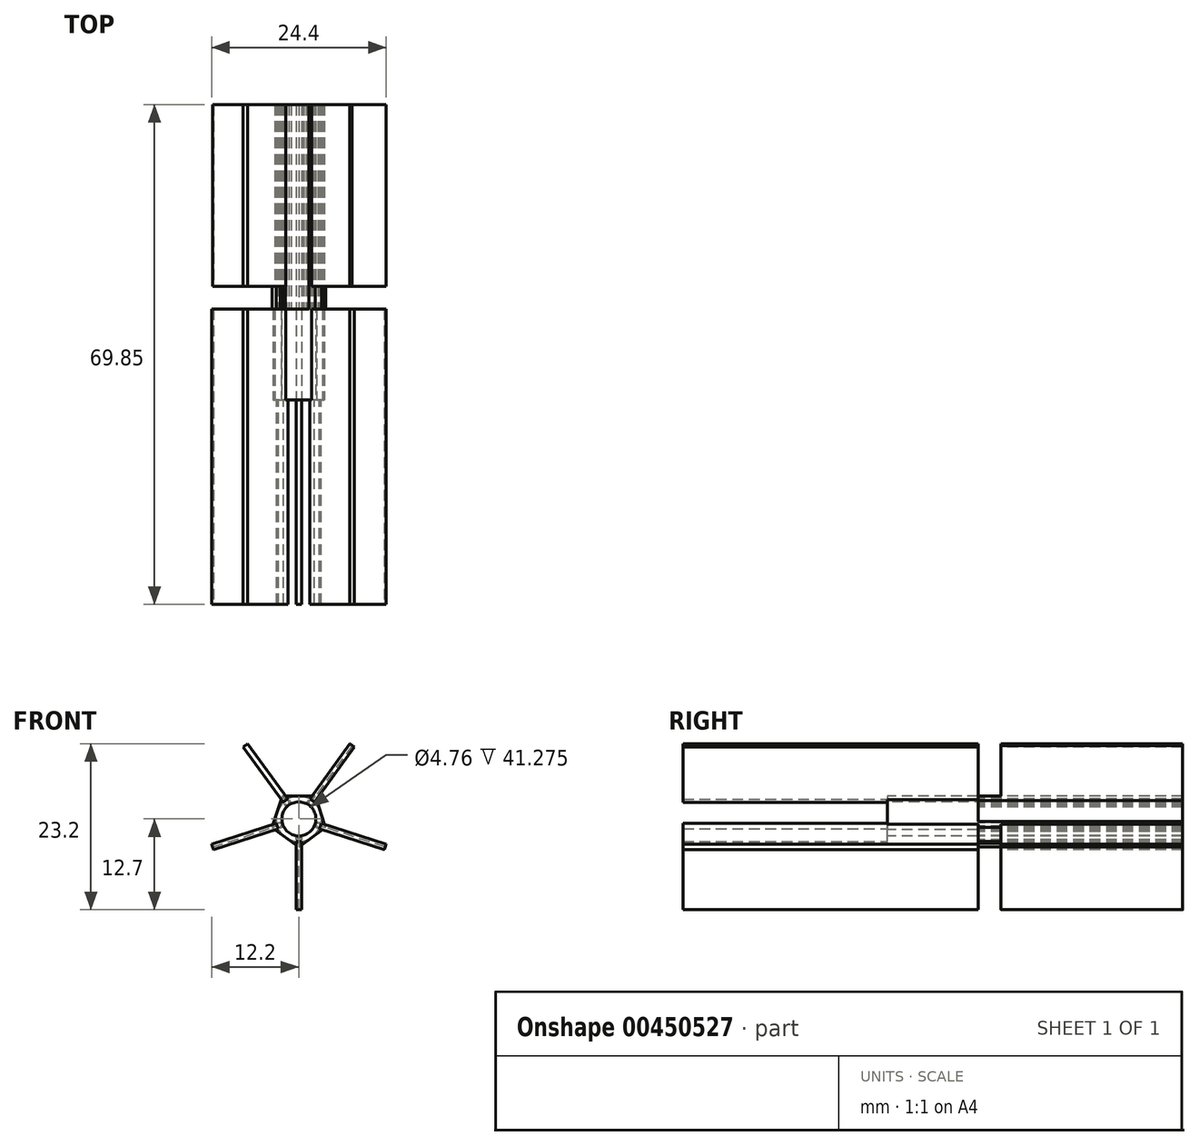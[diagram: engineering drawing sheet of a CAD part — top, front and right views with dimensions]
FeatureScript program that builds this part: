
annotation { "Feature Type Name" : "Feature", "Feature Type Description" : "" }
export const myFeature = defineFeature(function(context is Context, id is Id, definition is map)
    precondition{}
    {
        {
            var Q0;
            Q0=qCreatedBy(makeId("Front.planeOp"),FACE);
            var sketch = newSketch(context, id + "F0", { "sketchPlane" : qUnion([Q0])});
            skLineSegment(sketch, "E0", {"start": v(0, 0) * mm, "end": v(-7.46, 10.27) * mm});
            skLineSegment(sketch, "E1", {"start": v(0, 0) * mm, "end": v(7.46, 10.27) * mm});
            skArc(sketch, "E2", {"start": v(7.46, 10.27) * mm, "mid": v(0, 12.7) * mm, "end": v(-7.46, 10.27) * mm});
            skCircle(sketch, "E3", {"center": v(0, 7.62) * mm, "radius": 3.97 * mm});
            skCircle(sketch, "E4", {"center": v(0, 7.62) * mm, "radius": 3.66 * mm});
            skCircle(sketch, "E5", {"center": v(0, 7.62) * mm, "radius": 2.76 * mm});
            skLineSegment(sketch, "E6", {"start": v(3.41, 5.37) * mm, "end": v(7.14, 10.5) * mm});
            skLineSegment(sketch, "E7", {"start": v(3.41, 5.37) * mm, "end": v(0, 0.68) * mm});
            skLineSegment(sketch, "E8", {"start": v(-3.41, 5.37) * mm, "end": v(-7.14, 10.5) * mm});
            skLineSegment(sketch, "E9", {"start": v(-3.41, 5.37) * mm, "end": v(0, 0.68) * mm});
            skLineSegment(sketch, "E10", {"start": v(0, 3.17) * mm, "end": v(2.3, 3.17) * mm});
            skLineSegment(sketch, "E11", {"start": v(0, 3.17) * mm, "end": v(-2.3, 3.17) * mm});
            skLineSegment(sketch, "E12", {"start": v(0, 11.28) * mm, "end": v(5.84, 11.28) * mm});
            skLineSegment(sketch, "E13", {"start": v(0, 11.28) * mm, "end": v(-5.84, 11.28) * mm});
            skPoint(sketch, "E14.orphan", {"position": v(0, 12.7) * mm});
            skArc(sketch, "E15", {"start": v(1.87, 2.57) * mm, "mid": v(0, 3.17) * mm, "end": v(-1.87, 2.57) * mm});
            skArc(sketch, "E16", {"start": v(-5.6, 7.7) * mm, "mid": v(-4.37, 9.58) * mm, "end": v(-4.68, 11.8) * mm});
            skArc(sketch, "E17", {"start": v(4.68, 11.8) * mm, "mid": v(4.37, 9.58) * mm, "end": v(5.6, 7.7) * mm});
            skLineSegment(sketch, "E18", {"start": v(0, 7.62) * mm, "end": v(-5.54, 7.62) * mm});
            skLineSegment(sketch, "E19", {"start": v(0, 7.62) * mm, "end": v(5.54, 7.62) * mm});
            skArc(sketch, "E20", {"start": v(1.4, 1.93) * mm, "mid": v(0, 2.38) * mm, "end": v(-1.4, 1.93) * mm});
            skLineSegment(sketch, "E21", {"start": v(-1.4, 1.93) * mm, "end": v(-1.4, 3.17) * mm});
            skLineSegment(sketch, "E22", {"start": v(1.4, 1.93) * mm, "end": v(1.4, 3.17) * mm});
            skSolve(sketch);
        }
        {
            var Q0;
            Q0=qCreatedBy(makeId("Top.planeOp"),FACE);
            var sketch = newSketch(context, id + "F1", { "sketchPlane" : qUnion([Q0])});
            skLineSegment(sketch, "E23", {"start": v(0, 0) * mm, "end": v(0, 12.7) * mm});
            skSolve(sketch);
        }
        {
            var Q0;
            {var subQ0=sQuery(id+"F0.wireOp",EDGE,"E10");var subQ1=sQuery(id+"F0.wireOp",EDGE,"E1");var subQ2=makeQuery(id+"F0.imprint","INTERSECT",VERTEX,{"derivedFrom":[subQ1,subQ0]});Q0=makeQuery(id+"F0.imprint","IMPRINT",FACE,{"disambiguationData":[TD([[makeQuery(id+"F0.imprint","IMPRINT",EDGE,{"disambiguationData":[TD([[subQ2,-1.0]])],"derivedFrom":subQ1}),1.0]])]});}
            var Q1;
            {var subQ0=sQuery(id+"F0.wireOp",EDGE,"E11");var subQ1=sQuery(id+"F0.wireOp",EDGE,"E0");var subQ2=makeQuery(id+"F0.imprint","INTERSECT",VERTEX,{"derivedFrom":[subQ1,subQ0]});Q1=makeQuery(id+"F0.imprint","IMPRINT",FACE,{"disambiguationData":[TD([[makeQuery(id+"F0.imprint","IMPRINT",EDGE,{"disambiguationData":[TD([[subQ2,-1.0]])],"derivedFrom":subQ1}),-1.0]])]});}
            var Q2;
            {var subQ0=sQuery(id+"F0.wireOp",EDGE,"E10");var subQ1=sQuery(id+"F0.wireOp",EDGE,"E1");var subQ2=makeQuery(id+"F0.imprint","INTERSECT",VERTEX,{"derivedFrom":[subQ1,subQ0]});Q2=makeQuery(id+"F0.imprint","IMPRINT",FACE,{"disambiguationData":[TD([[makeQuery(id+"F0.imprint","IMPRINT",EDGE,{"disambiguationData":[TD([[subQ2,1.0]])],"derivedFrom":subQ1}),1.0]])]});}
            var Q3;
            {var subQ0=sQuery(id+"F0.wireOp",EDGE,"E10");var subQ1=sQuery(id+"F0.wireOp",EDGE,"E7");var subQ2=makeQuery(id+"F0.imprint","INTERSECT",VERTEX,{"derivedFrom":[subQ1,subQ0]});Q3=makeQuery(id+"F0.imprint","IMPRINT",FACE,{"disambiguationData":[TD([[makeQuery(id+"F0.imprint","IMPRINT",EDGE,{"disambiguationData":[TD([[subQ2,-1.0]])],"derivedFrom":subQ1}),-1.0]])]});}
            var Q4;
            {var subQ0=sQuery(id+"F0.wireOp",EDGE,"E11");var subQ1=sQuery(id+"F0.wireOp",EDGE,"E9");var subQ2=makeQuery(id+"F0.imprint","INTERSECT",VERTEX,{"derivedFrom":[subQ1,subQ0]});Q4=makeQuery(id+"F0.imprint","IMPRINT",FACE,{"disambiguationData":[TD([[makeQuery(id+"F0.imprint","IMPRINT",EDGE,{"disambiguationData":[TD([[subQ2,-1.0]])],"derivedFrom":subQ1}),1.0]])]});}
            var Q5;
            {var subQ0=sQuery(id+"F0.wireOp",EDGE,"E11");var subQ1=sQuery(id+"F0.wireOp",EDGE,"E0");var subQ2=makeQuery(id+"F0.imprint","INTERSECT",VERTEX,{"derivedFrom":[subQ1,subQ0]});Q5=makeQuery(id+"F0.imprint","IMPRINT",FACE,{"disambiguationData":[TD([[makeQuery(id+"F0.imprint","IMPRINT",EDGE,{"disambiguationData":[TD([[subQ2,1.0]])],"derivedFrom":subQ1}),-1.0]])]});}
            var Q6;
            {var subQ0=sQuery(id+"F0.wireOp",EDGE,"E15");var subQ1=sQuery(id+"F0.wireOp",EDGE,"E1");var subQ2=makeQuery(id+"F0.imprint","INTERSECT",VERTEX,{"derivedFrom":[subQ1,subQ0]});Q6=makeQuery(id+"F0.imprint","IMPRINT",FACE,{"disambiguationData":[TD([[makeQuery(id+"F0.imprint","IMPRINT",EDGE,{"disambiguationData":[TD([[subQ2,1.0]])],"derivedFrom":subQ1}),1.0]])]});}
            var Q7;
            {var subQ0=sQuery(id+"F0.wireOp",EDGE,"E15");var subQ6=sQuery(id+"F0.wireOp",EDGE,"E7");var subQ8=makeQuery(id+"F0.imprint","INTERSECT",VERTEX,{"derivedFrom":[subQ6,subQ0]});Q7=makeQuery(id+"F0.imprint","IMPRINT",FACE,{"disambiguationData":[TD([[makeQuery(id+"F0.imprint","IMPRINT",EDGE,{"disambiguationData":[TD([[subQ8,-1.0]])],"derivedFrom":subQ6}),-1.0]])]});}
            var Q8;
            {var subQ0=sQuery(id+"F0.wireOp",EDGE,"E15");var subQ1=sQuery(id+"F0.wireOp",EDGE,"E0");var subQ2=makeQuery(id+"F0.imprint","INTERSECT",VERTEX,{"derivedFrom":[subQ1,subQ0]});Q8=makeQuery(id+"F0.imprint","IMPRINT",FACE,{"disambiguationData":[TD([[makeQuery(id+"F0.imprint","IMPRINT",EDGE,{"disambiguationData":[TD([[subQ2,1.0]])],"derivedFrom":subQ1}),-1.0]])]});}
            var Q9;
            {var subQ0=sQuery(id+"F0.wireOp",EDGE,"E17");var subQ1=sQuery(id+"F0.wireOp",EDGE,"E1");var subQ2=makeQuery(id+"F0.imprint","INTERSECT",VERTEX,{"derivedFrom":[subQ1,subQ0]});Q9=makeQuery(id+"F0.imprint","IMPRINT",FACE,{"disambiguationData":[TD([[makeQuery(id+"F0.imprint","IMPRINT",EDGE,{"disambiguationData":[TD([[subQ2,1.0]])],"derivedFrom":subQ1}),1.0]])]});}
            var Q10;
            {var subQ0=sQuery(id+"F0.wireOp",EDGE,"E16");var subQ1=sQuery(id+"F0.wireOp",EDGE,"E0");var subQ2=makeQuery(id+"F0.imprint","INTERSECT",VERTEX,{"derivedFrom":[subQ1,subQ0]});Q10=makeQuery(id+"F0.imprint","IMPRINT",FACE,{"disambiguationData":[TD([[makeQuery(id+"F0.imprint","IMPRINT",EDGE,{"disambiguationData":[TD([[subQ2,1.0]])],"derivedFrom":subQ1}),-1.0]])]});}
            var Q11;
            {var subQ0=sQuery(id+"F0.wireOp",EDGE,"E15");var subQ1=sQuery(id+"F0.wireOp",EDGE,"E9");var subQ2=makeQuery(id+"F0.imprint","INTERSECT",VERTEX,{"derivedFrom":[subQ1,subQ0]});Q11=makeQuery(id+"F0.imprint","IMPRINT",FACE,{"disambiguationData":[TD([[makeQuery(id+"F0.imprint","IMPRINT",EDGE,{"disambiguationData":[TD([[subQ2,-1.0]])],"derivedFrom":subQ1}),1.0]])]});}
            var Q12;
            {var subQ0=sQuery(id+"F0.wireOp",EDGE,"E21");var subQ1=sQuery(id+"F0.wireOp",EDGE,"E9");var subQ2=makeQuery(id+"F0.imprint","INTERSECT",VERTEX,{"derivedFrom":[subQ1,subQ0]});Q12=makeQuery(id+"F0.imprint","IMPRINT",FACE,{"disambiguationData":[TD([[makeQuery(id+"F0.imprint","IMPRINT",EDGE,{"disambiguationData":[TD([[subQ2,-1.0]])],"derivedFrom":subQ1}),-1.0]])]});}
            var Q13;
            {var subQ0=sQuery(id+"F0.wireOp",EDGE,"E22");var subQ1=sQuery(id+"F0.wireOp",EDGE,"E7");var subQ2=makeQuery(id+"F0.imprint","INTERSECT",VERTEX,{"derivedFrom":[subQ1,subQ0]});Q13=makeQuery(id+"F0.imprint","IMPRINT",FACE,{"disambiguationData":[TD([[makeQuery(id+"F0.imprint","IMPRINT",EDGE,{"disambiguationData":[TD([[subQ2,-1.0]])],"derivedFrom":subQ1}),1.0]])]});}
            var Q14;
            {var subQ2=sQuery(id+"F0.wireOp",EDGE,"E22");var subQ10=sQuery(id+"F0.wireOp",EDGE,"E7");var subQ11=makeQuery(id+"F0.imprint","INTERSECT",VERTEX,{"derivedFrom":[subQ10,subQ2]});Q14=makeQuery(id+"F0.imprint","IMPRINT",FACE,{"disambiguationData":[TD([[makeQuery(id+"F0.imprint","IMPRINT",EDGE,{"disambiguationData":[TD([[subQ11,-1.0]])],"derivedFrom":subQ10}),-1.0]])]});}
            var Q15;
            {var subQ1=sQuery(id+"F0.wireOp",EDGE,"E11");var subQ3=sQuery(id+"F0.wireOp",EDGE,"E21");var subQ4=makeQuery(id+"F0.imprint","INTERSECT",VERTEX,{"derivedFrom":[subQ1,subQ3]});Q15=makeQuery(id+"F0.imprint","IMPRINT",FACE,{"disambiguationData":[TD([[makeQuery(id+"F0.imprint","IMPRINT",EDGE,{"disambiguationData":[TD([[subQ4,1.0]])],"derivedFrom":subQ3}),-1.0]])]});}
            var Q16;
            {var subQ1=sQuery(id+"F0.wireOp",EDGE,"E10");var subQ3=sQuery(id+"F0.wireOp",EDGE,"E22");var subQ4=makeQuery(id+"F0.imprint","INTERSECT",VERTEX,{"derivedFrom":[subQ1,subQ3]});Q16=makeQuery(id+"F0.imprint","IMPRINT",FACE,{"disambiguationData":[TD([[makeQuery(id+"F0.imprint","IMPRINT",EDGE,{"disambiguationData":[TD([[subQ4,1.0]])],"derivedFrom":subQ3}),1.0]])]});}
            var Q17;
            {var subQ0=sQuery(id+"F0.wireOp",EDGE,"E2");var subQ1=sQuery(id+"F0.wireOp",EDGE,"E1");var subQ2=makeQuery(id+"F0.imprint","INTERSECT",VERTEX,{"derivedFrom":[subQ1,subQ0]});Q17=makeQuery(id+"F0.imprint","IMPRINT",FACE,{"disambiguationData":[TD([[makeQuery(id+"F0.imprint","IMPRINT",EDGE,{"disambiguationData":[TD([[subQ2,1.0]])],"derivedFrom":subQ1}),1.0]])]});}
            var Q18;
            {var subQ0=sQuery(id+"F0.wireOp",EDGE,"E2");var subQ1=sQuery(id+"F0.wireOp",EDGE,"E0");var subQ2=makeQuery(id+"F0.imprint","INTERSECT",VERTEX,{"derivedFrom":[subQ1,subQ0]});Q18=makeQuery(id+"F0.imprint","IMPRINT",FACE,{"disambiguationData":[TD([[makeQuery(id+"F0.imprint","IMPRINT",EDGE,{"disambiguationData":[TD([[subQ2,1.0]])],"derivedFrom":subQ1}),-1.0]])]});}
            extrude(context, id + "F2", {"entities" : qUnion([Q0, Q1, Q2, Q3, Q4, Q5, Q6, Q7, Q8, Q9, Q10, Q11, Q12, Q13, Q14, Q15, Q16, Q17, Q18]), "oppositeDirection" : true, "depth" : 12.7 * mm});
        }
        {
            var Q0;
            {var subQ0=sQuery(id+"F0.wireOp",EDGE,"E11");var subQ1=sQuery(id+"F0.wireOp",EDGE,"E0");var subQ2=makeQuery(id+"F0.imprint","INTERSECT",VERTEX,{"derivedFrom":[subQ1,subQ0]});Q0=makeQuery(id+"F0.imprint","IMPRINT",FACE,{"disambiguationData":[TD([[makeQuery(id+"F0.imprint","IMPRINT",EDGE,{"disambiguationData":[TD([[subQ2,-1.0]])],"derivedFrom":subQ1}),-1.0]])]});}
            var Q1;
            {var subQ0=sQuery(id+"F0.wireOp",EDGE,"E11");var subQ1=sQuery(id+"F0.wireOp",EDGE,"E0");var subQ2=makeQuery(id+"F0.imprint","INTERSECT",VERTEX,{"derivedFrom":[subQ1,subQ0]});Q1=makeQuery(id+"F0.imprint","IMPRINT",FACE,{"disambiguationData":[TD([[makeQuery(id+"F0.imprint","IMPRINT",EDGE,{"disambiguationData":[TD([[subQ2,1.0]])],"derivedFrom":subQ1}),-1.0]])]});}
            var Q2;
            {var subQ0=sQuery(id+"F0.wireOp",EDGE,"E10");var subQ1=sQuery(id+"F0.wireOp",EDGE,"E1");var subQ2=makeQuery(id+"F0.imprint","INTERSECT",VERTEX,{"derivedFrom":[subQ1,subQ0]});Q2=makeQuery(id+"F0.imprint","IMPRINT",FACE,{"disambiguationData":[TD([[makeQuery(id+"F0.imprint","IMPRINT",EDGE,{"disambiguationData":[TD([[subQ2,1.0]])],"derivedFrom":subQ1}),1.0]])]});}
            var Q3;
            {var subQ3=sQuery(id+"F0.wireOp",EDGE,"E10");var subQ5=sQuery(id+"F0.wireOp",EDGE,"E1");var subQ6=makeQuery(id+"F0.imprint","INTERSECT",VERTEX,{"derivedFrom":[subQ5,subQ3]});Q3=makeQuery(id+"F0.imprint","IMPRINT",FACE,{"disambiguationData":[TD([[makeQuery(id+"F0.imprint","IMPRINT",EDGE,{"disambiguationData":[TD([[subQ6,-1.0]])],"derivedFrom":subQ5}),1.0]])]});}
            var Q4;
            {var subQ0=sQuery(id+"F0.wireOp",EDGE,"E17");var subQ1=sQuery(id+"F0.wireOp",EDGE,"E1");var subQ2=makeQuery(id+"F0.imprint","INTERSECT",VERTEX,{"derivedFrom":[subQ1,subQ0]});Q4=makeQuery(id+"F0.imprint","IMPRINT",FACE,{"disambiguationData":[TD([[makeQuery(id+"F0.imprint","IMPRINT",EDGE,{"disambiguationData":[TD([[subQ2,1.0]])],"derivedFrom":subQ1}),1.0]])]});}
            var Q5;
            {var subQ0=sQuery(id+"F0.wireOp",EDGE,"E16");var subQ1=sQuery(id+"F0.wireOp",EDGE,"E0");var subQ2=makeQuery(id+"F0.imprint","INTERSECT",VERTEX,{"derivedFrom":[subQ1,subQ0]});Q5=makeQuery(id+"F0.imprint","IMPRINT",FACE,{"disambiguationData":[TD([[makeQuery(id+"F0.imprint","IMPRINT",EDGE,{"disambiguationData":[TD([[subQ2,1.0]])],"derivedFrom":subQ1}),-1.0]])]});}
            var Q6;
            {var subQ0=sQuery(id+"F0.wireOp",EDGE,"E2");var subQ1=sQuery(id+"F0.wireOp",EDGE,"E0");var subQ2=makeQuery(id+"F0.imprint","INTERSECT",VERTEX,{"derivedFrom":[subQ1,subQ0]});Q6=makeQuery(id+"F0.imprint","IMPRINT",FACE,{"disambiguationData":[TD([[makeQuery(id+"F0.imprint","IMPRINT",EDGE,{"disambiguationData":[TD([[subQ2,1.0]])],"derivedFrom":subQ1}),-1.0]])]});}
            var Q7;
            {var subQ0=sQuery(id+"F0.wireOp",EDGE,"E2");var subQ1=sQuery(id+"F0.wireOp",EDGE,"E1");var subQ2=makeQuery(id+"F0.imprint","INTERSECT",VERTEX,{"derivedFrom":[subQ1,subQ0]});Q7=makeQuery(id+"F0.imprint","IMPRINT",FACE,{"disambiguationData":[TD([[makeQuery(id+"F0.imprint","IMPRINT",EDGE,{"disambiguationData":[TD([[subQ2,1.0]])],"derivedFrom":subQ1}),1.0]])]});}
            extrude(context, id + "F3", {"entities" : qUnion([Q0, Q1, Q2, Q3, Q4, Q5, Q6, Q7]), "operationType" : NewBodyOperationType.ADD, "depth" : 28.57 * mm});
        }
        {
            var Q0;
            Q0=makeQuery(id+"F2.opExtrude","CAP_FACE",FACE,{"disambiguationData":[OSD([sQuery(id+"F0.wireOp",EDGE,"E0"),sQuery(id+"F0.wireOp",EDGE,"E1"),sQuery(id+"F0.wireOp",EDGE,"E2"),sQuery(id+"F0.wireOp",EDGE,"E6"),sQuery(id+"F0.wireOp",EDGE,"E7"),sQuery(id+"F0.wireOp",EDGE,"E8"),sQuery(id+"F0.wireOp",EDGE,"E9"),sQuery(id+"F0.wireOp",EDGE,"E10"),sQuery(id+"F0.wireOp",EDGE,"E11"),sQuery(id+"F0.wireOp",EDGE,"E20")])],"isStart":false});
            var sketch = newSketch(context, id + "F4", { "sketchPlane" : qUnion([Q0])});
            skArc(sketch, "E24.0.0", {"start": v(-1.53, 2.78) * mm, "mid": v(-1.7, 2.68) * mm, "end": v(-1.87, 2.57) * mm});
            skLineSegment(sketch, "E24.0.1", {"start": v(-1.87, 2.57) * mm, "end": v(-2.3, 3.17) * mm});
            skLineSegment(sketch, "E24.0.2", {"start": v(-2.3, 3.17) * mm, "end": v(-1.82, 3.17) * mm});
            skLineSegment(sketch, "E24.0.3", {"start": v(-1.82, 3.17) * mm, "end": v(-1.53, 2.78) * mm});
            skLineSegment(sketch, "E25.0.0", {"start": v(-1.4, 3.17) * mm, "end": v(-1.4, 2.85) * mm});
            skArc(sketch, "E25.0.1", {"start": v(-1.4, 2.85) * mm, "mid": v(-1.47, 2.82) * mm, "end": v(-1.53, 2.78) * mm});
            skLineSegment(sketch, "E25.0.2", {"start": v(-1.53, 2.78) * mm, "end": v(-1.82, 3.17) * mm});
            skLineSegment(sketch, "E25.0.3", {"start": v(-1.82, 3.17) * mm, "end": v(-1.4, 3.17) * mm});
            skLineSegment(sketch, "E26.0.0", {"start": v(-1.4, 2.6) * mm, "end": v(-1.4, 2.85) * mm});
            skArc(sketch, "E26.0.1", {"start": v(-1.4, 2.85) * mm, "mid": v(-0.72, 3.1) * mm, "end": v(0, 3.18) * mm});
            skArc(sketch, "E26.0.2", {"start": v(0, 3.18) * mm, "mid": v(0.72, 3.1) * mm, "end": v(1.4, 2.85) * mm});
            skLineSegment(sketch, "E26.0.3", {"start": v(1.4, 2.85) * mm, "end": v(1.4, 2.6) * mm});
            skLineSegment(sketch, "E26.0.4", {"start": v(1.4, 2.6) * mm, "end": v(1.06, 2.13) * mm});
            skArc(sketch, "E26.0.5", {"start": v(1.06, 2.13) * mm, "mid": v(0, 2.38) * mm, "end": v(-1.06, 2.13) * mm});
            skLineSegment(sketch, "E26.0.6", {"start": v(-1.06, 2.13) * mm, "end": v(-1.4, 2.6) * mm});
            skArc(sketch, "E27.0.0", {"start": v(0, 3.18) * mm, "mid": v(-0.72, 3.1) * mm, "end": v(-1.4, 2.85) * mm});
            skLineSegment(sketch, "E27.0.1", {"start": v(-1.4, 2.85) * mm, "end": v(-1.4, 3.17) * mm});
            skLineSegment(sketch, "E27.0.2", {"start": v(-1.4, 3.17) * mm, "end": v(0, 3.17) * mm});
            skArc(sketch, "E28.0.0", {"start": v(1.4, 2.85) * mm, "mid": v(0.72, 3.1) * mm, "end": v(0, 3.18) * mm});
            skLineSegment(sketch, "E28.0.1", {"start": v(0, 3.17) * mm, "end": v(1.4, 3.17) * mm});
            skLineSegment(sketch, "E28.0.2", {"start": v(1.4, 3.17) * mm, "end": v(1.4, 2.85) * mm});
            skLineSegment(sketch, "E29.0.0", {"start": v(1.4, 2.85) * mm, "end": v(1.4, 3.17) * mm});
            skLineSegment(sketch, "E29.0.1", {"start": v(1.4, 3.17) * mm, "end": v(1.82, 3.17) * mm});
            skLineSegment(sketch, "E29.0.2", {"start": v(1.82, 3.17) * mm, "end": v(1.53, 2.78) * mm});
            skArc(sketch, "E29.0.3", {"start": v(1.53, 2.78) * mm, "mid": v(1.47, 2.82) * mm, "end": v(1.4, 2.85) * mm});
            skLineSegment(sketch, "E30.0.0", {"start": v(1.53, 2.78) * mm, "end": v(1.82, 3.17) * mm});
            skLineSegment(sketch, "E30.0.1", {"start": v(1.82, 3.17) * mm, "end": v(2.3, 3.17) * mm});
            skLineSegment(sketch, "E30.0.2", {"start": v(2.3, 3.17) * mm, "end": v(1.87, 2.57) * mm});
            skArc(sketch, "E30.0.3", {"start": v(1.87, 2.57) * mm, "mid": v(1.7, 2.68) * mm, "end": v(1.53, 2.78) * mm});
            skLineSegment(sketch, "E31.0.0", {"start": v(1.4, 2.6) * mm, "end": v(1.53, 2.78) * mm});
            skArc(sketch, "E31.0.1", {"start": v(1.53, 2.78) * mm, "mid": v(1.7, 2.68) * mm, "end": v(1.87, 2.57) * mm});
            skLineSegment(sketch, "E31.0.2", {"start": v(1.87, 2.57) * mm, "end": v(1.4, 1.93) * mm});
            skLineSegment(sketch, "E31.0.3", {"start": v(1.4, 1.93) * mm, "end": v(1.4, 2.6) * mm});
            skLineSegment(sketch, "E32.0.0", {"start": v(1.4, 2.6) * mm, "end": v(1.4, 1.93) * mm});
            skArc(sketch, "E32.0.1", {"start": v(1.4, 1.93) * mm, "mid": v(1.23, 2.04) * mm, "end": v(1.06, 2.13) * mm});
            skLineSegment(sketch, "E32.0.2", {"start": v(1.06, 2.13) * mm, "end": v(1.4, 2.6) * mm});
            skLineSegment(sketch, "E33.0.0", {"start": v(-1.4, 1.93) * mm, "end": v(-1.87, 2.57) * mm});
            skArc(sketch, "E33.0.1", {"start": v(-1.87, 2.57) * mm, "mid": v(-1.7, 2.68) * mm, "end": v(-1.53, 2.78) * mm});
            skLineSegment(sketch, "E33.0.2", {"start": v(-1.53, 2.78) * mm, "end": v(-1.4, 2.6) * mm});
            skLineSegment(sketch, "E33.0.3", {"start": v(-1.4, 2.6) * mm, "end": v(-1.4, 1.93) * mm});
            skLineSegment(sketch, "E34.0.0", {"start": v(-1.4, 1.93) * mm, "end": v(-1.4, 2.6) * mm});
            skLineSegment(sketch, "E34.0.1", {"start": v(-1.4, 2.6) * mm, "end": v(-1.06, 2.13) * mm});
            skArc(sketch, "E34.0.2", {"start": v(-1.06, 2.13) * mm, "mid": v(-1.23, 2.04) * mm, "end": v(-1.4, 1.93) * mm});
            skLineSegment(sketch, "E35.0.0", {"start": v(-7.14, 10.5) * mm, "end": v(-5.3, 7.96) * mm});
            skArc(sketch, "E35.0.1", {"start": v(-5.3, 7.96) * mm, "mid": v(-5.44, 7.83) * mm, "end": v(-5.6, 7.7) * mm});
            skLineSegment(sketch, "E35.0.2", {"start": v(-5.6, 7.7) * mm, "end": v(-7.46, 10.27) * mm});
            skArc(sketch, "E35.0.3", {"start": v(-7.46, 10.27) * mm, "mid": v(-7.3, 10.39) * mm, "end": v(-7.14, 10.5) * mm});
            skArc(sketch, "E36.0.0", {"start": v(-5.6, 7.7) * mm, "mid": v(-5.44, 7.83) * mm, "end": v(-5.3, 7.96) * mm});
            skLineSegment(sketch, "E36.0.1", {"start": v(-5.3, 7.96) * mm, "end": v(-5.05, 7.62) * mm});
            skLineSegment(sketch, "E36.0.2", {"start": v(-5.05, 7.62) * mm, "end": v(-5.54, 7.62) * mm});
            skLineSegment(sketch, "E36.0.3", {"start": v(-5.54, 7.62) * mm, "end": v(-5.6, 7.7) * mm});
            skLineSegment(sketch, "E37.0.0", {"start": v(-5.54, 7.62) * mm, "end": v(-5.05, 7.62) * mm});
            skLineSegment(sketch, "E37.0.1", {"start": v(-5.05, 7.62) * mm, "end": v(-3.41, 5.37) * mm});
            skLineSegment(sketch, "E37.0.2", {"start": v(-3.41, 5.37) * mm, "end": v(-1.82, 3.17) * mm});
            skLineSegment(sketch, "E37.0.3", {"start": v(-1.82, 3.17) * mm, "end": v(-2.3, 3.17) * mm});
            skLineSegment(sketch, "E37.0.4", {"start": v(-2.3, 3.17) * mm, "end": v(-5.54, 7.62) * mm});
            skLineSegment(sketch, "E38.0.0", {"start": v(7.46, 10.27) * mm, "end": v(5.6, 7.7) * mm});
            skArc(sketch, "E38.0.1", {"start": v(5.6, 7.7) * mm, "mid": v(5.44, 7.83) * mm, "end": v(5.3, 7.96) * mm});
            skLineSegment(sketch, "E38.0.2", {"start": v(5.3, 7.96) * mm, "end": v(7.14, 10.5) * mm});
            skArc(sketch, "E38.0.3", {"start": v(7.14, 10.5) * mm, "mid": v(7.3, 10.39) * mm, "end": v(7.46, 10.27) * mm});
            skArc(sketch, "E39.0.0", {"start": v(5.3, 7.96) * mm, "mid": v(5.44, 7.83) * mm, "end": v(5.6, 7.7) * mm});
            skLineSegment(sketch, "E39.0.1", {"start": v(5.6, 7.7) * mm, "end": v(5.54, 7.62) * mm});
            skLineSegment(sketch, "E39.0.2", {"start": v(5.54, 7.62) * mm, "end": v(5.05, 7.62) * mm});
            skLineSegment(sketch, "E39.0.3", {"start": v(5.05, 7.62) * mm, "end": v(5.3, 7.96) * mm});
            skLineSegment(sketch, "E40.0.0", {"start": v(2.3, 3.17) * mm, "end": v(1.82, 3.17) * mm});
            skLineSegment(sketch, "E40.0.1", {"start": v(1.82, 3.17) * mm, "end": v(3.41, 5.37) * mm});
            skLineSegment(sketch, "E40.0.2", {"start": v(3.41, 5.37) * mm, "end": v(5.05, 7.62) * mm});
            skLineSegment(sketch, "E40.0.3", {"start": v(5.05, 7.62) * mm, "end": v(5.54, 7.62) * mm});
            skLineSegment(sketch, "E40.0.4", {"start": v(5.54, 7.62) * mm, "end": v(2.3, 3.17) * mm});
            skSolve(sketch);
        }
        {
            var Q0;
            Q0=makeQuery(id+"F4.imprint","IMPRINT",FACE,{"disambiguationData":[TD([[makeQuery(id+"F4.imprint","IMPRINT",EDGE,{"derivedFrom":sQuery(id+"F4.wireOp",EDGE,"E33.0.0")}),-1.0]])]});
            var Q1;
            Q1=makeQuery(id+"F4.imprint","IMPRINT",FACE,{"disambiguationData":[TD([[makeQuery(id+"F4.imprint","IMPRINT",EDGE,{"derivedFrom":sQuery(id+"F4.wireOp",EDGE,"E26.0.0")}),-1.0]])]});
            var Q2;
            Q2=makeQuery(id+"F4.imprint","IMPRINT",FACE,{"disambiguationData":[TD([[makeQuery(id+"F4.imprint","IMPRINT",EDGE,{"derivedFrom":sQuery(id+"F4.wireOp",EDGE,"E31.0.0")}),-1.0]])]});
            var Q3;
            Q3=makeQuery(id+"F4.imprint","IMPRINT",FACE,{"disambiguationData":[TD([[makeQuery(id+"F4.imprint","IMPRINT",EDGE,{"derivedFrom":sQuery(id+"F4.wireOp",EDGE,"E34.0.0")}),-1.0]])]});
            var Q4;
            Q4=makeQuery(id+"F4.imprint","IMPRINT",FACE,{"disambiguationData":[TD([[makeQuery(id+"F4.imprint","IMPRINT",EDGE,{"derivedFrom":sQuery(id+"F4.wireOp",EDGE,"E25.0.1")}),1.0]])]});
            var Q5;
            Q5=makeQuery(id+"F4.imprint","IMPRINT",FACE,{"disambiguationData":[TD([[makeQuery(id+"F4.imprint","IMPRINT",EDGE,{"derivedFrom":sQuery(id+"F4.wireOp",EDGE,"E26.0.3")}),1.0]])]});
            var Q6;
            Q6=makeQuery(id+"F4.imprint","IMPRINT",FACE,{"disambiguationData":[TD([[makeQuery(id+"F4.imprint","IMPRINT",EDGE,{"derivedFrom":sQuery(id+"F4.wireOp",EDGE,"E32.0.0")}),-1.0]])]});
            var Q7;
            Q7=makeQuery(id+"F4.imprint","IMPRINT",FACE,{"disambiguationData":[TD([[makeQuery(id+"F4.imprint","IMPRINT",EDGE,{"derivedFrom":sQuery(id+"F4.wireOp",EDGE,"E24.0.1")}),-1.0]])]});
            var Q8;
            Q8=makeQuery(id+"F4.imprint","IMPRINT",FACE,{"disambiguationData":[TD([[makeQuery(id+"F4.imprint","IMPRINT",EDGE,{"derivedFrom":sQuery(id+"F4.wireOp",EDGE,"E25.0.1")}),-1.0]])]});
            var Q9;
            Q9=makeQuery(id+"F4.imprint","IMPRINT",FACE,{"disambiguationData":[TD([[makeQuery(id+"F4.imprint","IMPRINT",EDGE,{"derivedFrom":sQuery(id+"F4.wireOp",EDGE,"E27.0.0")}),-1.0]])]});
            var Q10;
            Q10=makeQuery(id+"F4.imprint","IMPRINT",FACE,{"disambiguationData":[TD([[makeQuery(id+"F4.imprint","IMPRINT",EDGE,{"derivedFrom":sQuery(id+"F4.wireOp",EDGE,"E28.0.0")}),-1.0]])]});
            var Q11;
            Q11=makeQuery(id+"F4.imprint","IMPRINT",FACE,{"disambiguationData":[TD([[makeQuery(id+"F4.imprint","IMPRINT",EDGE,{"derivedFrom":sQuery(id+"F4.wireOp",EDGE,"E29.0.0")}),-1.0]])]});
            var Q12;
            Q12=makeQuery(id+"F4.imprint","IMPRINT",FACE,{"disambiguationData":[TD([[makeQuery(id+"F4.imprint","IMPRINT",EDGE,{"derivedFrom":sQuery(id+"F4.wireOp",EDGE,"E30.0.0")}),-1.0]])]});
            extrude(context, id + "F5", {"entities" : qUnion([Q0, Q1, Q2, Q3, Q4, Q5, Q6, Q7, Q8, Q9, Q10, Q11, Q12]), "operationType" : NewBodyOperationType.ADD, "depth" : 3.17 * mm});
        }
        {
            var Q0;
            Q0=makeQuery(id+"F5.opExtrude","CAP_FACE",FACE,{"disambiguationData":[OSD([sQuery(id+"F4.wireOp",EDGE,"E24.0.1"),sQuery(id+"F4.wireOp",EDGE,"E25.0.3"),sQuery(id+"F4.wireOp",EDGE,"E26.0.5"),sQuery(id+"F4.wireOp",EDGE,"E27.0.2"),sQuery(id+"F4.wireOp",EDGE,"E28.0.1"),sQuery(id+"F4.wireOp",EDGE,"E29.0.1"),sQuery(id+"F4.wireOp",EDGE,"E30.0.2"),sQuery(id+"F4.wireOp",EDGE,"E31.0.2"),sQuery(id+"F4.wireOp",EDGE,"E32.0.1"),sQuery(id+"F4.wireOp",EDGE,"E33.0.0"),sQuery(id+"F4.wireOp",EDGE,"E34.0.2"),sQuery(id+"F4.wireOp",EDGE,"E37.0.3"),sQuery(id+"F4.wireOp",EDGE,"E40.0.0")])],"isStart":false});
            var sketch = newSketch(context, id + "F6", { "sketchPlane" : qUnion([Q0])});
            skLineSegment(sketch, "E41.0.0", {"start": v(-2.3, 3.17) * mm, "end": v(-1.82, 3.17) * mm});
            skLineSegment(sketch, "E41.0.1", {"start": v(-1.82, 3.17) * mm, "end": v(-7.14, 10.5) * mm});
            skArc(sketch, "E41.0.2", {"start": v(-7.14, 10.5) * mm, "mid": v(-7.3, 10.39) * mm, "end": v(-7.46, 10.27) * mm});
            skLineSegment(sketch, "E41.0.3", {"start": v(-7.46, 10.27) * mm, "end": v(-2.3, 3.17) * mm});
            skLineSegment(sketch, "E42.0.0", {"start": v(1.82, 3.17) * mm, "end": v(2.3, 3.17) * mm});
            skLineSegment(sketch, "E42.0.1", {"start": v(2.3, 3.17) * mm, "end": v(7.46, 10.27) * mm});
            skArc(sketch, "E42.0.2", {"start": v(7.46, 10.27) * mm, "mid": v(7.3, 10.39) * mm, "end": v(7.14, 10.5) * mm});
            skLineSegment(sketch, "E42.0.3", {"start": v(7.14, 10.5) * mm, "end": v(1.82, 3.17) * mm});
            skLineSegment(sketch, "E43.0.0", {"start": v(-2.3, 3.17) * mm, "end": v(-1.4, 1.93) * mm});
            skArc(sketch, "E43.0.1", {"start": v(-1.4, 1.93) * mm, "mid": v(0, 2.38) * mm, "end": v(1.4, 1.93) * mm});
            skLineSegment(sketch, "E43.0.2", {"start": v(1.4, 1.93) * mm, "end": v(2.3, 3.17) * mm});
            skLineSegment(sketch, "E43.0.3", {"start": v(2.3, 3.17) * mm, "end": v(-2.3, 3.17) * mm});
            skSolve(sketch);
        }
        {
            var Q0;
            {var subQ0=sQuery(id+"F6.wireOp",EDGE,"E41.0.1");Q0=makeQuery(id+"F6.imprint","IMPRINT",FACE,{"disambiguationData":[TD([[makeQuery(id+"F6.imprint","IMPRINT",EDGE,{"derivedFrom":subQ0}),1.0]])]});}
            var Q1;
            {var subQ3=sQuery(id+"F6.wireOp",EDGE,"E43.0.0");Q1=makeQuery(id+"F6.imprint","IMPRINT",FACE,{"disambiguationData":[TD([[makeQuery(id+"F6.imprint","IMPRINT",EDGE,{"derivedFrom":subQ3}),-1.0]])]});}
            var Q2;
            {var subQ0=sQuery(id+"F6.wireOp",EDGE,"E42.0.1");Q2=makeQuery(id+"F6.imprint","IMPRINT",FACE,{"disambiguationData":[TD([[makeQuery(id+"F6.imprint","IMPRINT",EDGE,{"derivedFrom":subQ0}),1.0]])]});}
            extrude(context, id + "F7", {"entities" : qUnion([Q0, Q1, Q2]), "operationType" : NewBodyOperationType.ADD, "depth" : 25.4 * mm});
        }
        {
            var Q0;
            Q0=makeQuery(id+"F2.opExtrude","SWEPT_BODY",BODY,{"disambiguationData":[OSD([sQuery(id+"F0.wireOp",EDGE,"E0"),sQuery(id+"F0.wireOp",EDGE,"E1"),sQuery(id+"F0.wireOp",EDGE,"E6"),sQuery(id+"F0.wireOp",EDGE,"E7"),sQuery(id+"F0.wireOp",EDGE,"E8"),sQuery(id+"F0.wireOp",EDGE,"E9"),sQuery(id+"F0.wireOp",EDGE,"E10"),sQuery(id+"F0.wireOp",EDGE,"E11"),sQuery(id+"F0.wireOp",EDGE,"E16"),sQuery(id+"F0.wireOp",EDGE,"E17")])]});
            var Q1;
            Q1=sQuery(id+"F1.wireOp",EDGE,"E23");
            circularPattern(context, id + "F8", {"operationType" : NewBodyOperationType.ADD, "entities" : qUnion([Q0]), "axis" : qUnion([Q1]), "angle" : 360 * degree, "instanceCount" : 5, "equalSpace" : true, "computeTransformsWithoutBuiltin" : true});
        }
    });
